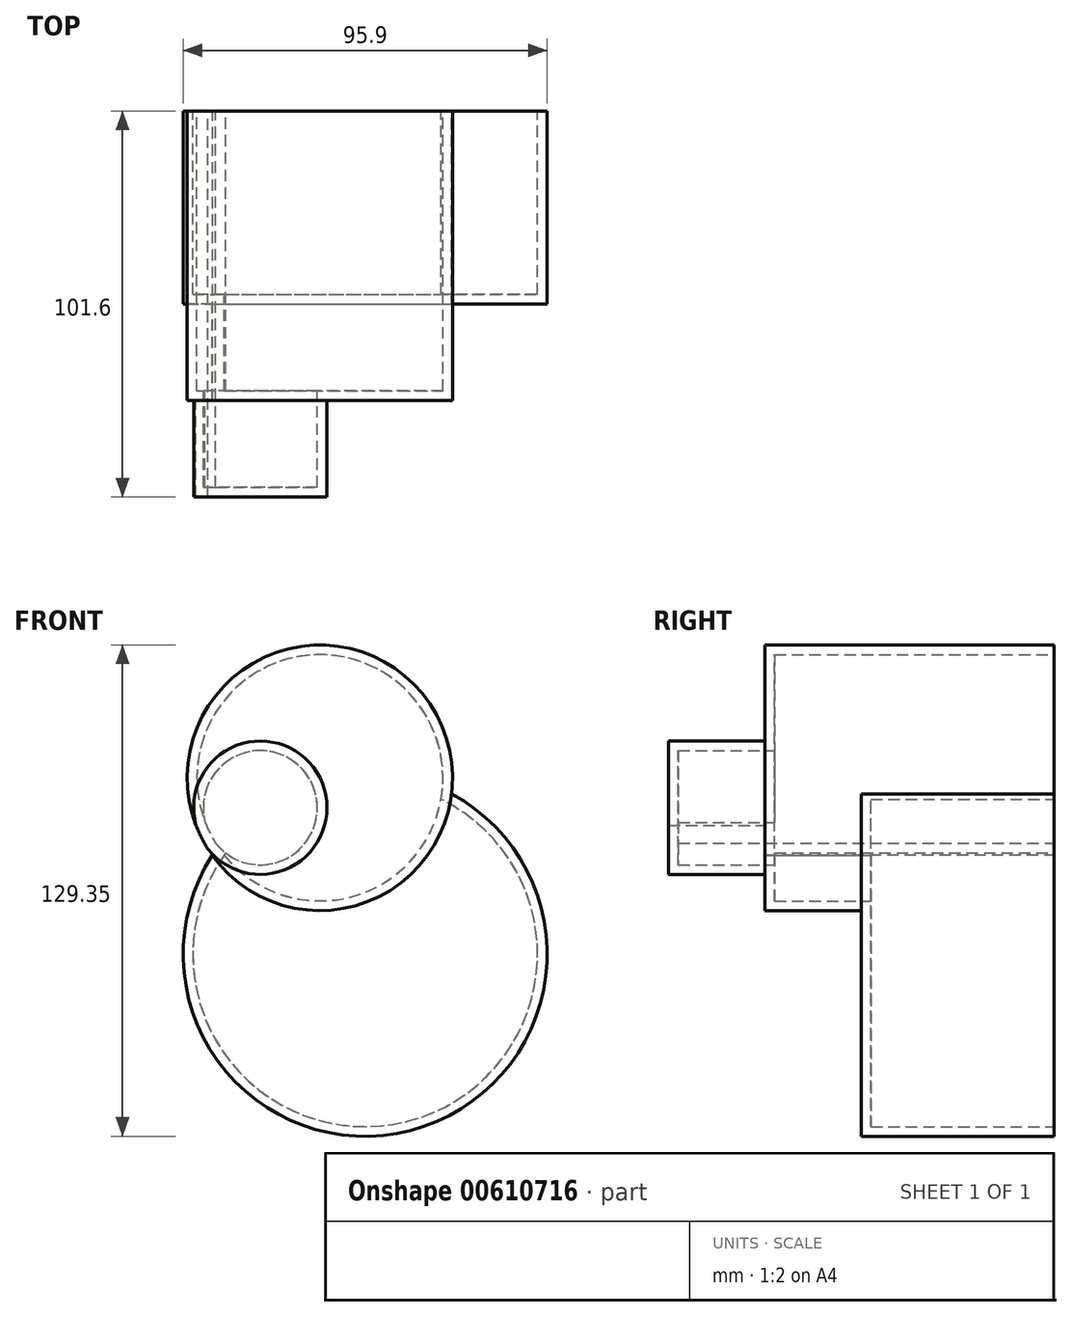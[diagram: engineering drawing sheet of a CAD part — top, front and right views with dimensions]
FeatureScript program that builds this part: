
annotation { "Feature Type Name" : "Feature", "Feature Type Description" : "" }
export const myFeature = defineFeature(function(context is Context, id is Id, definition is map)
    precondition{}
    {
        {
            var Q0;
            Q0=qCreatedBy(makeId("Front.planeOp"),FACE);
            var sketch = newSketch(context, id + "F0", { "sketchPlane" : qUnion([Q0])});
            skCircle(sketch, "E0", {"center": v(-10.5, 23.74) * mm, "radius": 17.57 * mm});
            skCircle(sketch, "E1", {"center": v(17.13, -14.82) * mm, "radius": 47.95 * mm});
            skCircle(sketch, "E2", {"center": v(5.2, 31.62) * mm, "radius": 34.96 * mm});
            skSolve(sketch);
        }
        {
            var Q0;
            {var subQ0=sQuery(id+"F0.wireOp",EDGE,"E2");var subQ1=sQuery(id+"F0.wireOp",EDGE,"E0");var subQ2=makeQuery(id+"F0.imprint","INTERSECT",VERTEX,{"disambiguationData":[OD(0.0)],"derivedFrom":[subQ1,subQ0]});Q0=makeQuery(id+"F0.imprint","IMPRINT",FACE,{"disambiguationData":[TD([[makeQuery(id+"F0.imprint","IMPRINT",EDGE,{"disambiguationData":[TD([[subQ2,1.0]])],"derivedFrom":subQ1}),1.0]])]});}
            var Q1;
            {var subQ0=sQuery(id+"F0.wireOp",EDGE,"E1");var subQ1=sQuery(id+"F0.wireOp",EDGE,"E0");var subQ2=makeQuery(id+"F0.imprint","INTERSECT",VERTEX,{"disambiguationData":[OD(0.0)],"derivedFrom":[subQ1,subQ0]});Q1=makeQuery(id+"F0.imprint","IMPRINT",FACE,{"disambiguationData":[TD([[makeQuery(id+"F0.imprint","IMPRINT",EDGE,{"disambiguationData":[TD([[subQ2,1.0]])],"derivedFrom":subQ1}),1.0]])]});}
            extrude(context, id + "F1", {"entities" : qUnion([Q0, Q1]), "depth" : 101.6 * mm, "offsetDistance" : 25.4 * mm});
        }
        {
            var Q0;
            {var subQ0=sQuery(id+"F0.wireOp",EDGE,"E2");var subQ1=sQuery(id+"F0.wireOp",EDGE,"E0");var subQ2=makeQuery(id+"F0.imprint","INTERSECT",VERTEX,{"disambiguationData":[OD(0.0)],"derivedFrom":[subQ1,subQ0]});Q0=makeQuery(id+"F0.imprint","IMPRINT",FACE,{"disambiguationData":[TD([[makeQuery(id+"F0.imprint","IMPRINT",EDGE,{"disambiguationData":[TD([[subQ2,1.0]])],"derivedFrom":subQ1}),-1.0]])]});}
            var Q1;
            {var subQ0=sQuery(id+"F0.wireOp",EDGE,"E1");var subQ1=sQuery(id+"F0.wireOp",EDGE,"E0");var subQ2=makeQuery(id+"F0.imprint","INTERSECT",VERTEX,{"disambiguationData":[OD(0.0)],"derivedFrom":[subQ1,subQ0]});Q1=makeQuery(id+"F0.imprint","IMPRINT",FACE,{"disambiguationData":[TD([[makeQuery(id+"F0.imprint","IMPRINT",EDGE,{"disambiguationData":[TD([[subQ2,1.0]])],"derivedFrom":subQ1}),-1.0]])]});}
            extrude(context, id + "F2", {"entities" : qUnion([Q0, Q1]), "operationType" : NewBodyOperationType.ADD, "depth" : 76.2 * mm, "offsetDistance" : 25.4 * mm});
        }
        {
            var Q0;
            {var subQ0=sQuery(id+"F0.wireOp",EDGE,"E2");var subQ1=sQuery(id+"F0.wireOp",EDGE,"E1");var subQ2=makeQuery(id+"F0.imprint","INTERSECT",VERTEX,{"disambiguationData":[OD(0.0)],"derivedFrom":[subQ1,subQ0]});Q0=makeQuery(id+"F0.imprint","IMPRINT",FACE,{"disambiguationData":[TD([[makeQuery(id+"F0.imprint","IMPRINT",EDGE,{"disambiguationData":[TD([[subQ2,1.0]])],"derivedFrom":subQ1}),1.0]])]});}
            extrude(context, id + "F3", {"entities" : qUnion([Q0]), "operationType" : NewBodyOperationType.ADD, "depth" : 50.8 * mm, "offsetDistance" : 25.4 * mm});
        }
        {
            var Q0;
            {var subQ0=sQuery(id+"F0.wireOp",EDGE,"E2");var subQ1=sQuery(id+"F0.wireOp",EDGE,"E1");var subQ2=sQuery(id+"F0.wireOp",EDGE,"E0");Q0=makeQuery(id+"F3.boolean.opBoolean","MERGE",FACE,{"derivedFrom":[makeQuery(id+"F2.boolean.opBoolean","MERGE",FACE,{"derivedFrom":[makeQuery(id+"F1.opExtrude","CAP_FACE",FACE,{"disambiguationData":[OSD([subQ2,subQ0])],"isStart":true}),makeQuery(id+"F2.opExtrude","CAP_FACE",FACE,{"disambiguationData":[OSD([subQ2,subQ1,subQ0])],"isStart":true})]}),makeQuery(id+"F3.opExtrude","CAP_FACE",FACE,{"disambiguationData":[OSD([subQ1,subQ0])],"isStart":true})]});}
            shell(context, id + "F4", {"entities" : qUnion([Q0]), "thickness" : 2.54 * mm});
        }
    });
